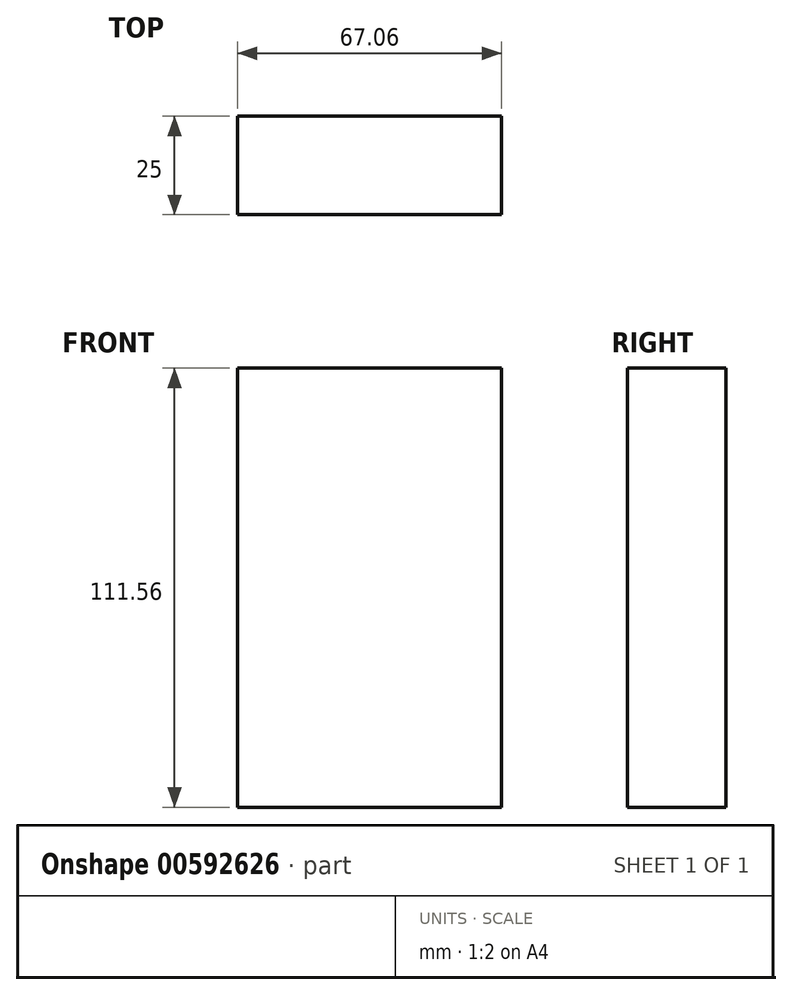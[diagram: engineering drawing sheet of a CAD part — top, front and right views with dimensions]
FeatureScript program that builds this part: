
annotation { "Feature Type Name" : "Feature", "Feature Type Description" : "" }
export const myFeature = defineFeature(function(context is Context, id is Id, definition is map)
    precondition{}
    {
        {
            var Q0;
            Q0=qCreatedBy(makeId("Front.planeOp"),FACE);
            var sketch = newSketch(context, id + "F0", { "sketchPlane" : qUnion([Q0])});
            skLineSegment(sketch, "E0.bottom", {"start": v(-33.53, 55.78) * mm, "end": v(33.53, 55.78) * mm});
            skLineSegment(sketch, "E0.top", {"start": v(-33.53, -55.78) * mm, "end": v(33.53, -55.78) * mm});
            skLineSegment(sketch, "E0.left", {"start": v(-33.53, 55.78) * mm, "end": v(-33.53, -55.78) * mm});
            skLineSegment(sketch, "E0.right", {"start": v(33.53, 55.78) * mm, "end": v(33.53, -55.78) * mm});
            skPoint(sketch, "E0.middle", {"position": v(0, 0) * mm});
            skSolve(sketch);
        }
        {
            var Q0;
            Q0=makeQuery(id+"F0.imprint","IMPRINT",FACE,{"disambiguationData":[TD([[makeQuery(id+"F0.imprint","IMPRINT",EDGE,{"derivedFrom":sQuery(id+"F0.wireOp",EDGE,"E0.bottom")}),-1.0]])]});
            extrude(context, id + "F1", {"entities" : qUnion([Q0]), "depth" : 25 * mm, "offsetDistance" : 25 * mm});
        }
    });
